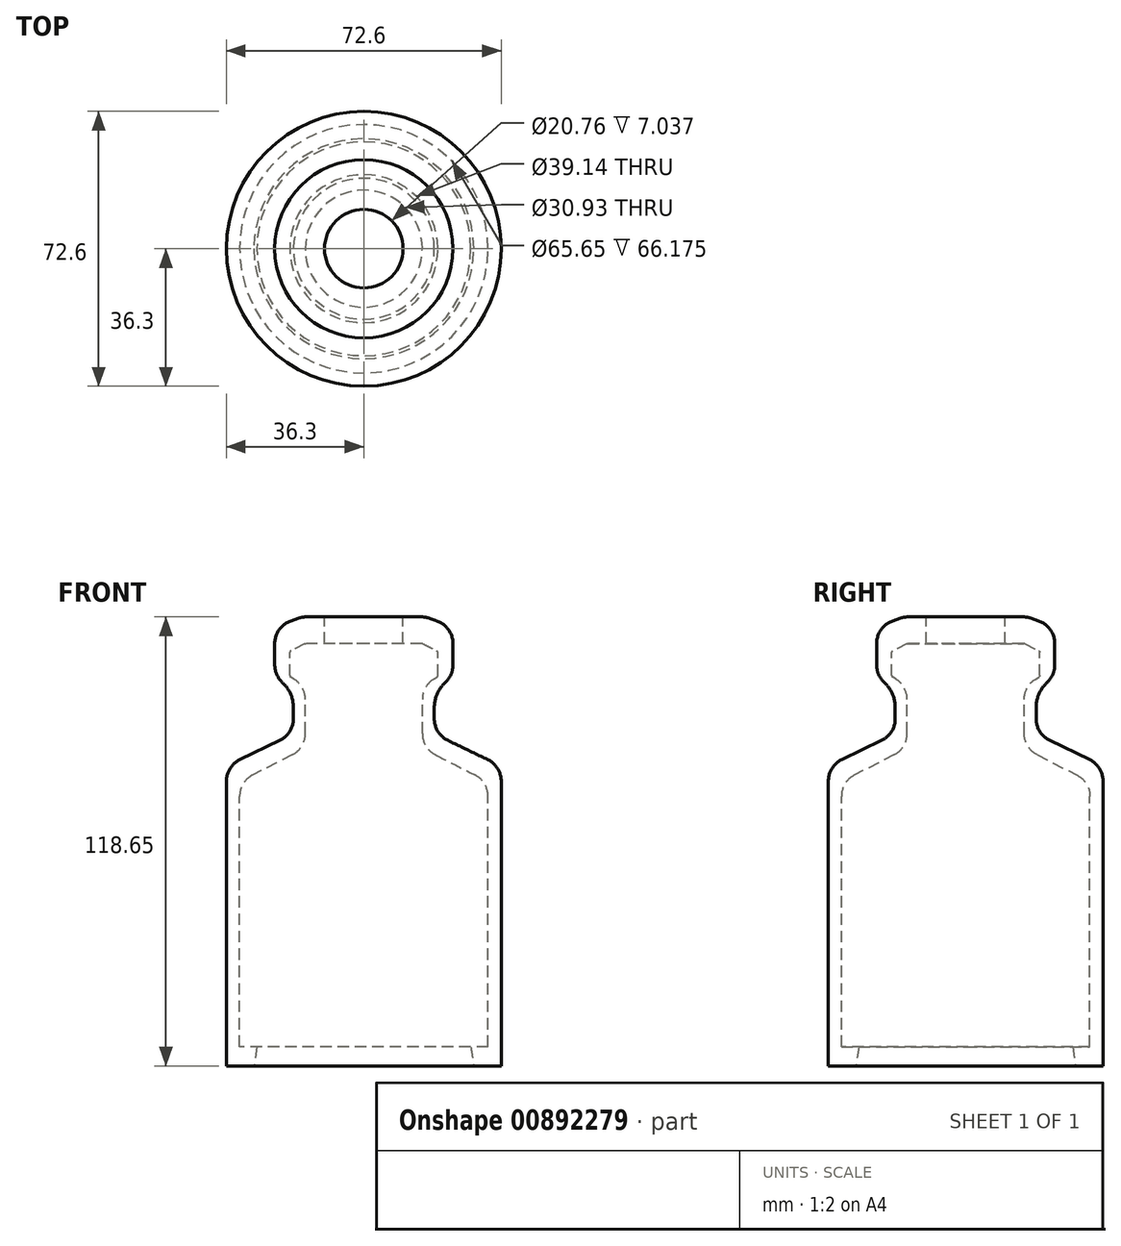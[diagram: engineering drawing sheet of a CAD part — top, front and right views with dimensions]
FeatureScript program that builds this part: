
annotation { "Feature Type Name" : "Feature", "Feature Type Description" : "" }
export const myFeature = defineFeature(function(context is Context, id is Id, definition is map)
    precondition{}
    {
        {
            var Q0;
            Q0=qCreatedBy(makeId("Front.planeOp"),FACE);
            var sketch = newSketch(context, id + "F0", { "sketchPlane" : qUnion([Q0])});
            skLineSegment(sketch, "E0", {"start": v(0, -59.34) * mm, "end": v(0, -54.29) * mm});
            skLineSegment(sketch, "E1", {"start": v(0, -54.29) * mm, "end": v(32.82, -54.29) * mm});
            skLineSegment(sketch, "E2", {"start": v(32.82, -54.29) * mm, "end": v(32.82, 11.89) * mm});
            skLineSegment(sketch, "E3", {"start": v(29.36, 17.55) * mm, "end": v(18.93, 22.85) * mm});
            skLineSegment(sketch, "E4", {"start": v(15.47, 28.51) * mm, "end": v(15.47, 37.48) * mm});
            skLineSegment(sketch, "E5", {"start": v(18.49, 42.9) * mm, "end": v(19.36, 43.43) * mm});
            skLineSegment(sketch, "E6", {"start": v(19.57, 43.8) * mm, "end": v(19.57, 49.92) * mm});
            skLineSegment(sketch, "E7", {"start": v(19.33, 50.3) * mm, "end": v(15.56, 52.23) * mm});
            skLineSegment(sketch, "E8", {"start": v(15.36, 52.27) * mm, "end": v(10.38, 52.27) * mm});
            skLineSegment(sketch, "E9", {"start": v(0, 52.27) * mm, "end": v(0, -59.34) * mm});
            skLineSegment(sketch, "E10", {"start": v(10.38, 59.3) * mm, "end": v(15.2, 59.3) * mm});
            skLineSegment(sketch, "E11", {"start": v(17.3, 58.96) * mm, "end": v(19.28, 58.27) * mm});
            skLineSegment(sketch, "E12", {"start": v(23.54, 52.27) * mm, "end": v(23.54, 46.62) * mm});
            skLineSegment(sketch, "E13", {"start": v(21.5, 41.96) * mm, "end": v(21.48, 41.94) * mm});
            skLineSegment(sketch, "E14", {"start": v(18.62, 35.4) * mm, "end": v(18.62, 32.4) * mm});
            skLineSegment(sketch, "E15", {"start": v(22.21, 26.67) * mm, "end": v(32.7, 21.62) * mm});
            skLineSegment(sketch, "E16", {"start": v(36.3, 15.9) * mm, "end": v(36.3, -59.34) * mm});
            skLineSegment(sketch, "E17", {"start": v(36.3, -59.34) * mm, "end": v(0, -59.34) * mm});
            skPoint(sketch, "E18.orphan", {"position": v(0, -61.23) * mm});
            skPoint(sketch, "E19.visualSharp", {"position": v(32.82, 15.78) * mm});
            skArc(sketch, "E19.filletArc", {"start": v(32.82, 11.89) * mm, "mid": v(31.89, 15.2) * mm, "end": v(29.36, 17.55) * mm});
            skPoint(sketch, "E20.visualSharp", {"position": v(15.47, 24.62) * mm});
            skArc(sketch, "E20.filletArc", {"start": v(15.47, 28.51) * mm, "mid": v(16.4, 25.2) * mm, "end": v(18.93, 22.85) * mm});
            skPoint(sketch, "E21.visualSharp", {"position": v(15.47, 41.03) * mm});
            skArc(sketch, "E21.filletArc", {"start": v(18.49, 42.9) * mm, "mid": v(16.27, 40.58) * mm, "end": v(15.47, 37.48) * mm});
            skPoint(sketch, "E22.visualSharp", {"position": v(36.3, 19.88) * mm});
            skArc(sketch, "E22.filletArc", {"start": v(36.3, 15.9) * mm, "mid": v(35.32, 19.27) * mm, "end": v(32.7, 21.62) * mm});
            skPoint(sketch, "E23.visualSharp", {"position": v(18.62, 28.4) * mm});
            skArc(sketch, "E23.filletArc", {"start": v(18.62, 32.4) * mm, "mid": v(19.6, 29.02) * mm, "end": v(22.21, 26.67) * mm});
            skPoint(sketch, "E24.visualSharp", {"position": v(18.62, 39.3) * mm});
            skArc(sketch, "E24.filletArc", {"start": v(21.48, 41.94) * mm, "mid": v(19.37, 38.98) * mm, "end": v(18.62, 35.4) * mm});
            skPoint(sketch, "E25.visualSharp", {"position": v(23.54, 43.84) * mm});
            skArc(sketch, "E25.filletArc", {"start": v(21.5, 41.96) * mm, "mid": v(23, 44.08) * mm, "end": v(23.54, 46.62) * mm});
            skPoint(sketch, "E26.visualSharp", {"position": v(19.57, 43.56) * mm});
            skArc(sketch, "E26.filletArc", {"start": v(19.36, 43.43) * mm, "mid": v(19.51, 43.59) * mm, "end": v(19.57, 43.8) * mm});
            skPoint(sketch, "E27.visualSharp", {"position": v(19.57, 50.18) * mm});
            skArc(sketch, "E27.filletArc", {"start": v(19.57, 49.92) * mm, "mid": v(19.5, 50.14) * mm, "end": v(19.33, 50.3) * mm});
            skPoint(sketch, "E28.visualSharp", {"position": v(15.47, 52.27) * mm});
            skArc(sketch, "E28.filletArc", {"start": v(15.56, 52.23) * mm, "mid": v(15.46, 52.26) * mm, "end": v(15.36, 52.27) * mm});
            skPoint(sketch, "E29.visualSharp", {"position": v(16.28, 59.3) * mm});
            skArc(sketch, "E29.filletArc", {"start": v(17.3, 58.96) * mm, "mid": v(16.27, 59.22) * mm, "end": v(15.2, 59.3) * mm});
            skPoint(sketch, "E30.visualSharp", {"position": v(23.54, 56.78) * mm});
            skArc(sketch, "E30.filletArc", {"start": v(23.54, 52.27) * mm, "mid": v(22.37, 55.95) * mm, "end": v(19.28, 58.27) * mm});
            skPoint(sketch, "E31.end.orphan", {"position": v(-17.68, 57.44) * mm});
            skLineSegment(sketch, "E32", {"start": v(10.38, 52.27) * mm, "end": v(10.38, 59.3) * mm});
            skPoint(sketch, "E33.start.orphan", {"position": v(0, 57.44) * mm});
            skSolve(sketch);
        }
        {
            var Q0;
            Q0 = qSketchRegion(id + "F0", true);
            var Q1;
            Q1=sQuery(id+"F0.wireOp",EDGE,"E9");
            revolve(context, id + "F1", {"surfaceOperationType" : NewSurfaceOperationType.NEW, "entities" : qUnion([Q0]), "axis" : qUnion([Q1]), "revolveType" : RevolveType.FULL});
        }
        {
            var Q0;
            Q0=makeQuery(id+"F1.opRevolve","SWEPT_FACE",FACE,{"disambiguationData":[OSD([sQuery(id+"F0.wireOp",EDGE,"E17")])]});
            var sketch = newSketch(context, id + "F2", { "sketchPlane" : qUnion([Q0])});
            skCircle(sketch, "E34", {"center": v(0, 0) * mm, "radius": 29.06 * mm});
            skSolve(sketch);
        }
        {
            var Q0;
            Q0 = qSketchRegion(id + "F2", true);
            extrude(context, id + "F3", {"entities" : qUnion([Q0]), "operationType" : NewBodyOperationType.REMOVE, "oppositeDirection" : true, "depth" : 25.4 * mm, "offsetDistance" : 25.4 * mm, "hasDraft" : true, "draftAngle" : 9 * degree, "draftPullDirection" : true});
        }
    });
